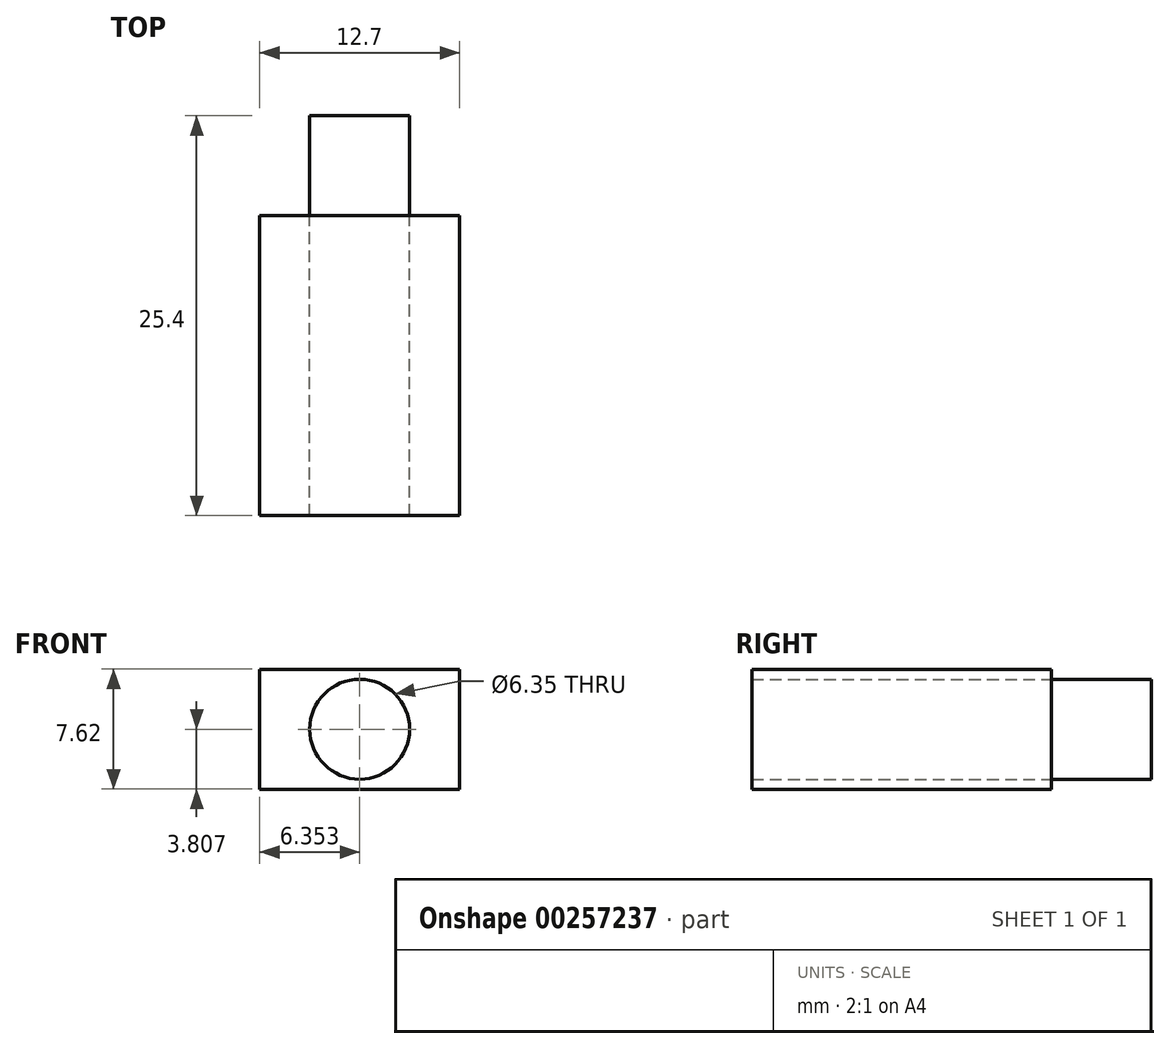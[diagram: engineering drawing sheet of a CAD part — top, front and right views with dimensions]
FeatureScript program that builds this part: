
annotation { "Feature Type Name" : "Feature", "Feature Type Description" : "" }
export const myFeature = defineFeature(function(context is Context, id is Id, definition is map)
    precondition{}
    {
        {
            var Q0;
            Q0=qCreatedBy(makeId("Front.planeOp"),FACE);
            var sketch = newSketch(context, id + "F0", { "sketchPlane" : qUnion([Q0])});
            skCircle(sketch, "E0", {"center": v(-9.82, 15.22) * mm, "radius": 3.18 * mm});
            skSolve(sketch);
        }
        {
            var Q0;
            Q0 = qSketchRegion(id + "F0", true);
            extrude(context, id + "F1", {"entities" : qUnion([Q0]), "depth" : 6.35 * mm});
        }
        {
            var Q0;
            Q0=makeQuery(id+"F1.opExtrude","CAP_FACE",FACE,{"disambiguationData":[OSD([sQuery(id+"F0.wireOp",EDGE,"E0")])],"isStart":false});
            var sketch = newSketch(context, id + "F2", { "sketchPlane" : qUnion([Q0])});
            skLineSegment(sketch, "E1.bottom", {"start": v(-16.17, 19.03) * mm, "end": v(-3.47, 19.03) * mm});
            skLineSegment(sketch, "E1.top", {"start": v(-16.17, 11.4) * mm, "end": v(-3.47, 11.4) * mm});
            skLineSegment(sketch, "E1.left", {"start": v(-16.17, 19.03) * mm, "end": v(-16.17, 11.4) * mm});
            skLineSegment(sketch, "E1.right", {"start": v(-3.47, 19.03) * mm, "end": v(-3.47, 11.4) * mm});
            skPoint(sketch, "E1.middle", {"position": v(-9.82, 15.22) * mm});
            skSolve(sketch);
        }
        {
            var Q0;
            Q0=makeQuery(id+"F2.imprint","IMPRINT",FACE,{"disambiguationData":[TD([[makeQuery(id+"F2.imprint","IMPRINT",EDGE,{"derivedFrom":sQuery(id+"F2.wireOp",EDGE,"E1.bottom")}),-1.0]])]});
            extrude(context, id + "F3", {"entities" : qUnion([Q0]), "depth" : 19.05 * mm});
        }
    });
